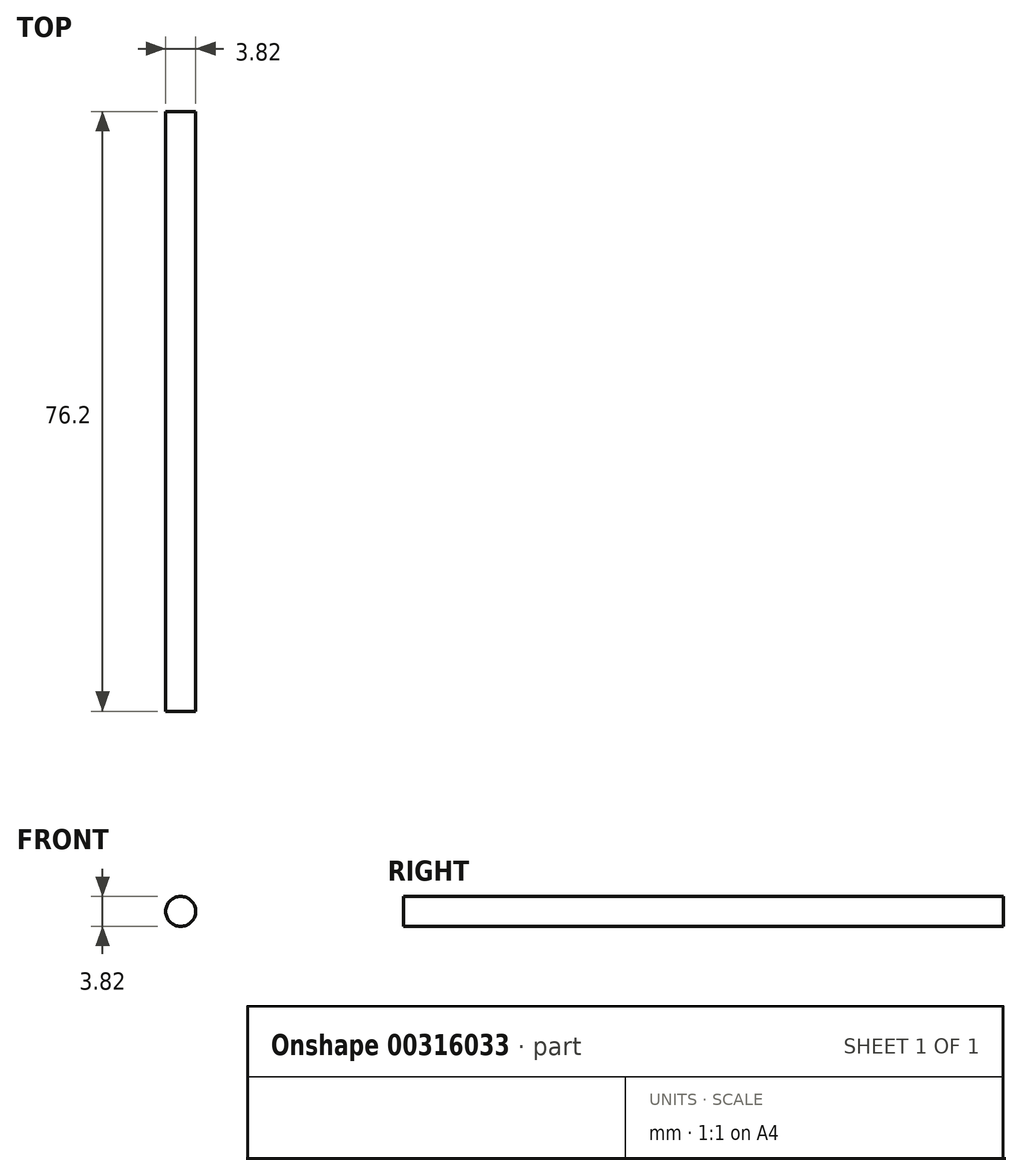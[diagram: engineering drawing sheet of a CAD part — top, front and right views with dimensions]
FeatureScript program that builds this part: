
annotation { "Feature Type Name" : "Feature", "Feature Type Description" : "" }
export const myFeature = defineFeature(function(context is Context, id is Id, definition is map)
    precondition{}
    {
        {
            var Q0;
            Q0=qCreatedBy(makeId("Front.planeOp"),FACE);
            var sketch = newSketch(context, id + "F0", { "sketchPlane" : qUnion([Q0])});
            skCircle(sketch, "E0", {"center": v(0, 0) * mm, "radius": 1.9 * mm});
            skSolve(sketch);
        }
        {
            var Q0;
            Q0 = qSketchRegion(id + "F0", true);
            extrude(context, id + "F1", {"entities" : qUnion([Q0]), "depth" : 76.2 * mm});
        }
    });
